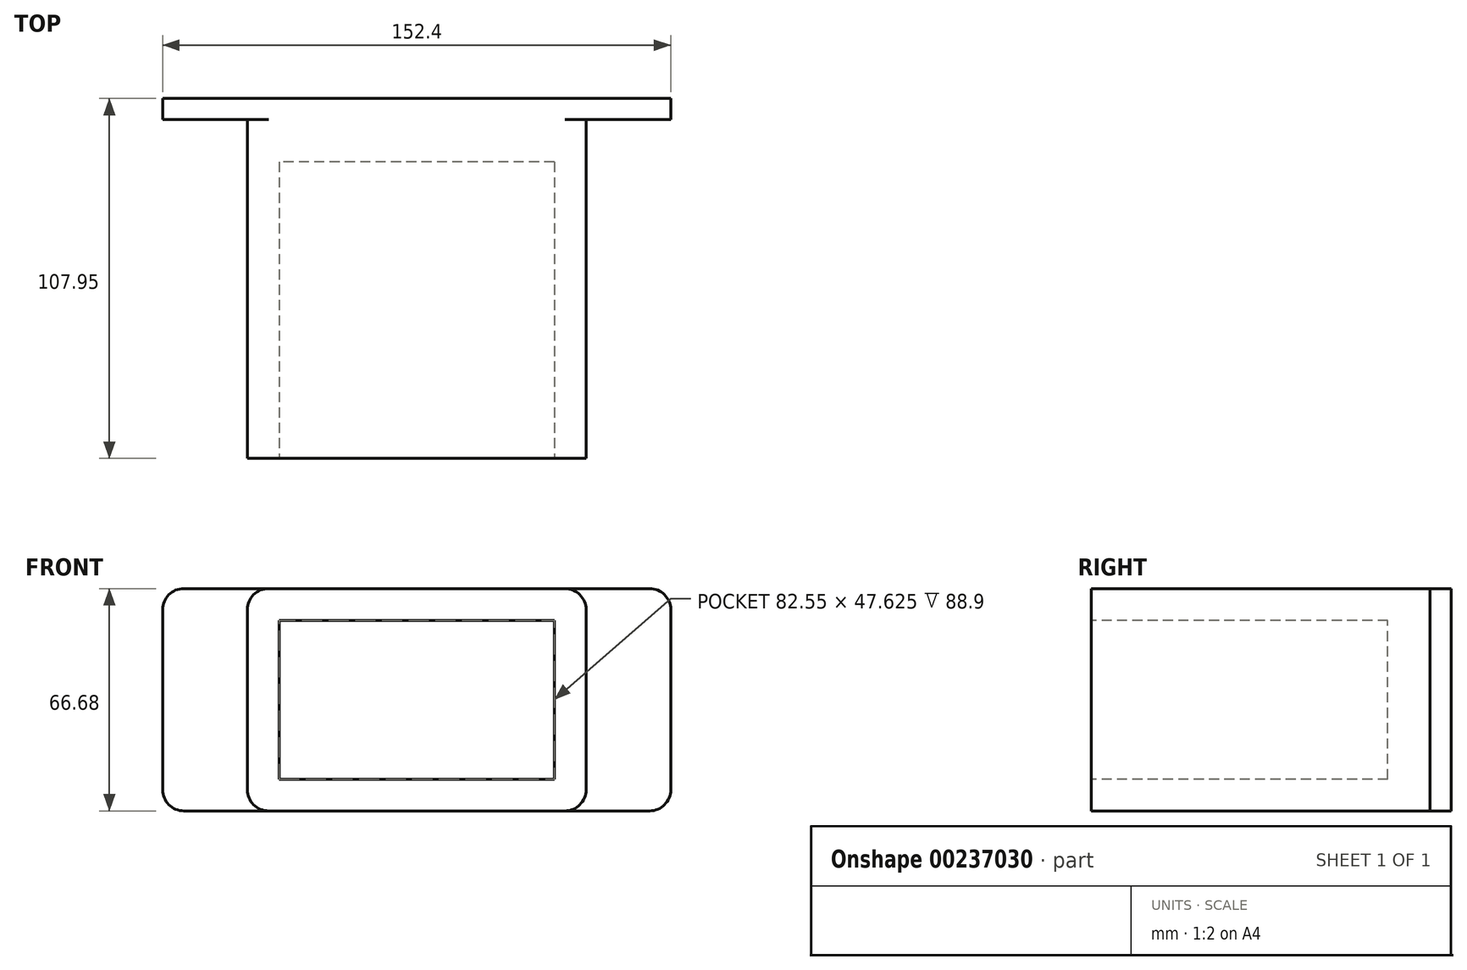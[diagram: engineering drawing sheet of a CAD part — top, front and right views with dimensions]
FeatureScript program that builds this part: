
annotation { "Feature Type Name" : "Feature", "Feature Type Description" : "" }
export const myFeature = defineFeature(function(context is Context, id is Id, definition is map)
    precondition{}
    {
        {
            var Q0;
            Q0=qCreatedBy(makeId("Front.planeOp"),FACE);
            var sketch = newSketch(context, id + "F0", { "sketchPlane" : qUnion([Q0])});
            skLineSegment(sketch, "E0.bottom", {"start": v(76.2, 33.34) * mm, "end": v(-76.2, 33.34) * mm});
            skLineSegment(sketch, "E0.top", {"start": v(76.2, -33.34) * mm, "end": v(-76.2, -33.34) * mm});
            skLineSegment(sketch, "E0.left", {"start": v(76.2, 33.34) * mm, "end": v(76.2, -33.34) * mm});
            skLineSegment(sketch, "E0.right", {"start": v(-76.2, 33.34) * mm, "end": v(-76.2, -33.34) * mm});
            skPoint(sketch, "E0.middle", {"position": v(0, 0) * mm});
            skSolve(sketch);
        }
        {
            var Q0;
            Q0=makeQuery(id+"F0.imprint","IMPRINT",FACE,{"disambiguationData":[TD([[makeQuery(id+"F0.imprint","IMPRINT",EDGE,{"derivedFrom":sQuery(id+"F0.wireOp",EDGE,"E0.bottom")}),1.0]])]});
            extrude(context, id + "F1", {"entities" : qUnion([Q0]), "depth" : 6.35 * mm});
        }
        {
            var Q0;
            Q0=makeQuery(id+"F1.opExtrude","CAP_FACE",FACE,{"disambiguationData":[OSD([sQuery(id+"F0.wireOp",EDGE,"E0.bottom"),sQuery(id+"F0.wireOp",EDGE,"E0.top"),sQuery(id+"F0.wireOp",EDGE,"E0.left"),sQuery(id+"F0.wireOp",EDGE,"E0.right")])],"isStart":false});
            var sketch = newSketch(context, id + "F2", { "sketchPlane" : qUnion([Q0])});
            skLineSegment(sketch, "E1.bottom", {"start": v(50.8, 33.34) * mm, "end": v(-50.8, 33.34) * mm});
            skLineSegment(sketch, "E1.top", {"start": v(50.8, -33.34) * mm, "end": v(-50.8, -33.34) * mm});
            skLineSegment(sketch, "E1.left", {"start": v(50.8, 33.34) * mm, "end": v(50.8, -33.34) * mm});
            skLineSegment(sketch, "E1.right", {"start": v(-50.8, 33.34) * mm, "end": v(-50.8, -33.34) * mm});
            skPoint(sketch, "E1.middle", {"position": v(0, 0) * mm});
            skSolve(sketch);
        }
        {
            var Q0;
            Q0 = qSketchRegion(id + "F2", true);
            extrude(context, id + "F3", {"entities" : qUnion([Q0]), "operationType" : NewBodyOperationType.ADD, "depth" : 101.6 * mm});
        }
        {
            var Q0;
            Q0=makeQuery(id+"F1.opExtrude","SWEPT_EDGE",EDGE,{"disambiguationData":[OSD([sQuery(id+"F0.wireOp",EDGE,"E0.top"),sQuery(id+"F0.wireOp",EDGE,"E0.left")])]});
            var Q1;
            Q1=makeQuery(id+"F1.opExtrude","SWEPT_EDGE",EDGE,{"disambiguationData":[OSD([sQuery(id+"F0.wireOp",EDGE,"E0.bottom"),sQuery(id+"F0.wireOp",EDGE,"E0.left")])]});
            var Q2;
            Q2=makeQuery(id+"F1.opExtrude","SWEPT_EDGE",EDGE,{"disambiguationData":[OSD([sQuery(id+"F0.wireOp",EDGE,"E0.bottom"),sQuery(id+"F0.wireOp",EDGE,"E0.right")])]});
            var Q3;
            Q3=makeQuery(id+"F1.opExtrude","SWEPT_EDGE",EDGE,{"disambiguationData":[OSD([sQuery(id+"F0.wireOp",EDGE,"E0.top"),sQuery(id+"F0.wireOp",EDGE,"E0.right")])]});
            var Q4;
            Q4=makeQuery(id+"F3.opExtrude","SWEPT_EDGE",EDGE,{"disambiguationData":[OSD([sQuery(id+"F0.wireOp",EDGE,"E0.top"),sQuery(id+"F2.wireOp",EDGE,"E1.top"),sQuery(id+"F2.wireOp",EDGE,"E1.left")])]});
            var Q5;
            Q5=makeQuery(id+"F3.opExtrude","SWEPT_EDGE",EDGE,{"disambiguationData":[OSD([sQuery(id+"F0.wireOp",EDGE,"E0.bottom"),sQuery(id+"F2.wireOp",EDGE,"E1.bottom"),sQuery(id+"F2.wireOp",EDGE,"E1.left")])]});
            var Q6;
            Q6=makeQuery(id+"F3.opExtrude","SWEPT_EDGE",EDGE,{"disambiguationData":[OSD([sQuery(id+"F0.wireOp",EDGE,"E0.bottom"),sQuery(id+"F2.wireOp",EDGE,"E1.bottom"),sQuery(id+"F2.wireOp",EDGE,"E1.right")])]});
            var Q7;
            Q7=makeQuery(id+"F3.opExtrude","SWEPT_EDGE",EDGE,{"disambiguationData":[OSD([sQuery(id+"F0.wireOp",EDGE,"E0.top"),sQuery(id+"F2.wireOp",EDGE,"E1.top"),sQuery(id+"F2.wireOp",EDGE,"E1.right")])]});
            fillet(context, id + "F4", {"entities" : qUnion([Q0, Q1, Q2, Q3, Q4, Q5, Q6, Q7]), "radius" : 6.35 * mm, "tangentPropagation" : true, "allowEdgeOverflow" : false});
        }
        {
            var Q0;
            Q0=makeQuery(id+"F3.opExtrude","CAP_FACE",FACE,{"disambiguationData":[OSD([sQuery(id+"F2.wireOp",EDGE,"E1.bottom"),sQuery(id+"F2.wireOp",EDGE,"E1.top"),sQuery(id+"F2.wireOp",EDGE,"E1.left"),sQuery(id+"F2.wireOp",EDGE,"E1.right")])],"isStart":false});
            var sketch = newSketch(context, id + "F5", { "sketchPlane" : qUnion([Q0])});
            skLineSegment(sketch, "E2.bottom", {"start": v(41.28, -23.81) * mm, "end": v(-41.27, -23.81) * mm});
            skLineSegment(sketch, "E2.top", {"start": v(41.28, 23.81) * mm, "end": v(-41.27, 23.81) * mm});
            skLineSegment(sketch, "E2.left", {"start": v(41.28, -23.81) * mm, "end": v(41.28, 23.81) * mm});
            skLineSegment(sketch, "E2.right", {"start": v(-41.27, -23.81) * mm, "end": v(-41.27, 23.81) * mm});
            skPoint(sketch, "E2.middle", {"position": v(0, 0) * mm});
            skSolve(sketch);
        }
        {
            var Q0;
            Q0 = qSketchRegion(id + "F5", true);
            extrude(context, id + "F6", {"entities" : qUnion([Q0]), "operationType" : NewBodyOperationType.REMOVE, "oppositeDirection" : true, "depth" : 88.9 * mm});
        }
    });
